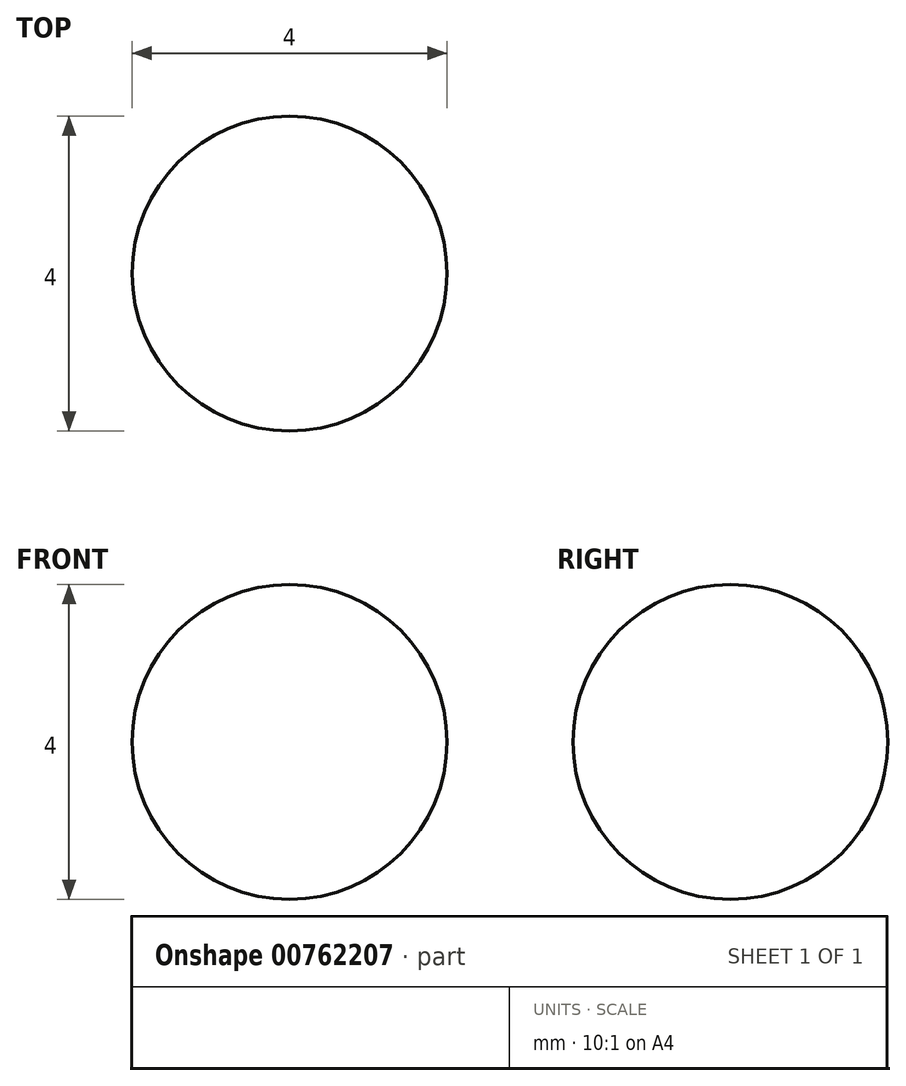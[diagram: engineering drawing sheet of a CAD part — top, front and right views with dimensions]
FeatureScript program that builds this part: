
annotation { "Feature Type Name" : "Feature", "Feature Type Description" : "" }
export const myFeature = defineFeature(function(context is Context, id is Id, definition is map)
    precondition{}
    {
        {
            var Q0;
            Q0=qCreatedBy(makeId("Right.planeOp"),FACE);
            var sketch = newSketch(context, id + "F0", { "sketchPlane" : qUnion([Q0])});
            skArc(sketch, "E0", {"start": v(0, 2) * mm, "mid": v(-2, 0) * mm, "end": v(0, -2) * mm});
            skLineSegment(sketch, "E1", {"start": v(0, -2.99) * mm, "end": v(0, 3.03) * mm, "construction": true});
            skLineSegment(sketch, "E2", {"start": v(0, 2) * mm, "end": v(0, -2) * mm});
            skSolve(sketch);
        }
        {
            var Q0;
            Q0=makeQuery(id+"F0.imprint","IMPRINT",FACE,{"disambiguationData":[TD([[makeQuery(id+"F0.imprint","IMPRINT",EDGE,{"derivedFrom":sQuery(id+"F0.wireOp",EDGE,"E0")}),1.0]])]});
            var Q1;
            Q1=sQuery(id+"F0.wireOp",EDGE,"E1");
            revolve(context, id + "F1", {"surfaceOperationType" : NewSurfaceOperationType.NEW, "entities" : qUnion([Q0]), "axis" : qUnion([Q1]), "revolveType" : RevolveType.FULL});
        }
    });
